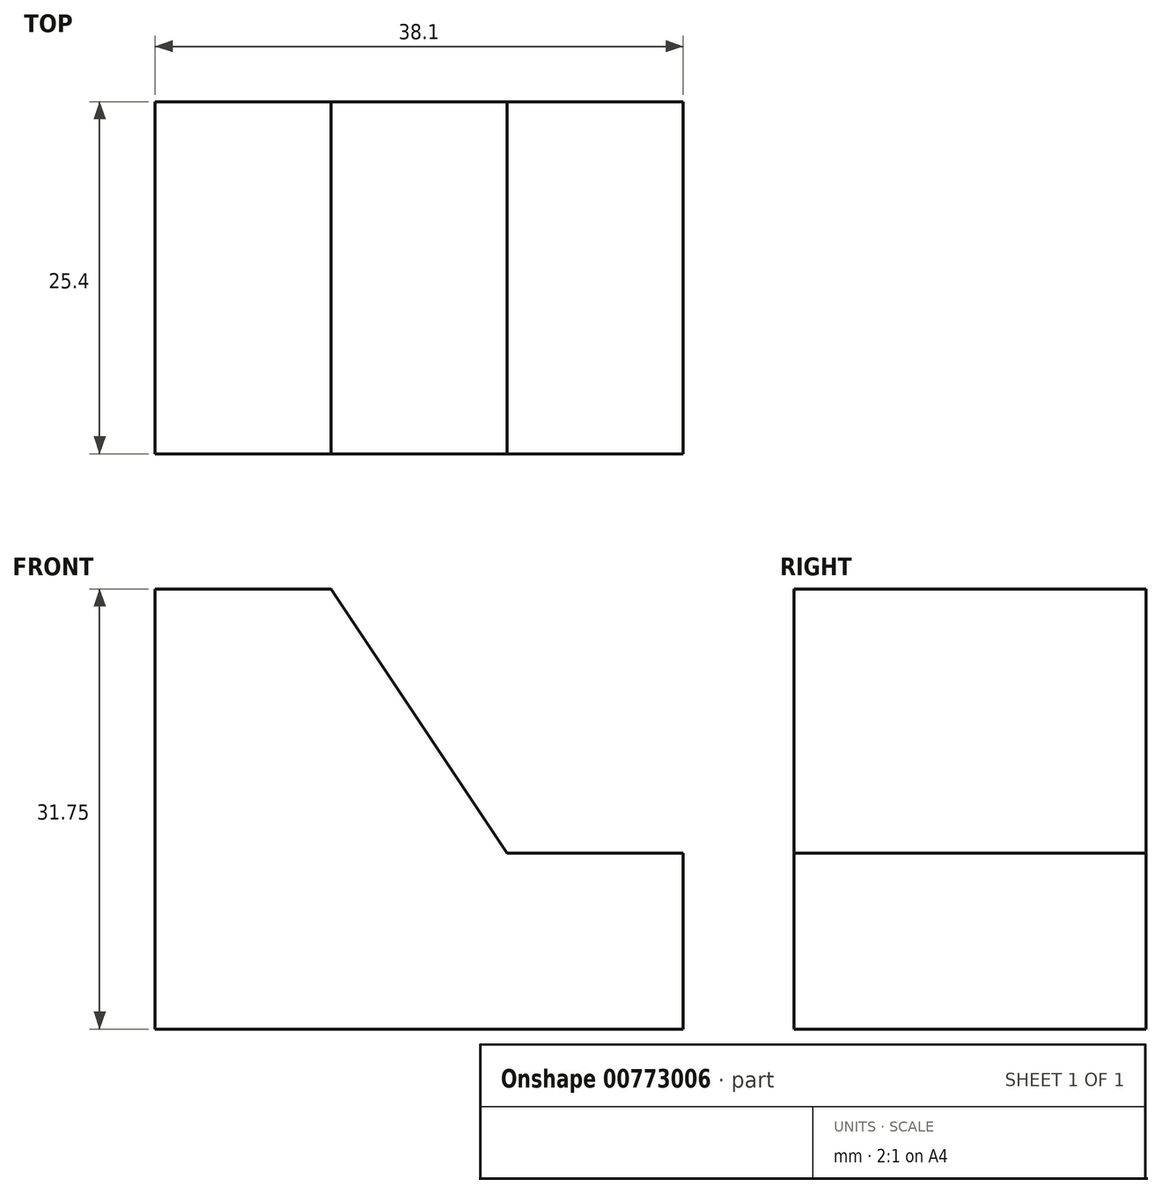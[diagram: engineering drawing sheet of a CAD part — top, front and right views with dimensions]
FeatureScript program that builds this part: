
annotation { "Feature Type Name" : "Feature", "Feature Type Description" : "" }
export const myFeature = defineFeature(function(context is Context, id is Id, definition is map)
    precondition{}
    {
        {
            var Q0;
            Q0=qCreatedBy(makeId("Front.planeOp"),FACE);
            var sketch = newSketch(context, id + "F0", { "sketchPlane" : qUnion([Q0])});
            skLineSegment(sketch, "E0", {"start": v(0, 0) * mm, "end": v(38.1, 0) * mm});
            skLineSegment(sketch, "E1", {"start": v(38.1, 0) * mm, "end": v(38.1, 31.75) * mm});
            skLineSegment(sketch, "E2", {"start": v(38.1, 31.75) * mm, "end": v(0, 31.75) * mm});
            skLineSegment(sketch, "E3", {"start": v(0, 31.75) * mm, "end": v(0, 0) * mm});
            skSolve(sketch);
        }
        {
            var Q0;
            Q0=makeQuery(id+"F0.imprint","IMPRINT",FACE,{"disambiguationData":[TD([[makeQuery(id+"F0.imprint","IMPRINT",EDGE,{"derivedFrom":sQuery(id+"F0.wireOp",EDGE,"E0")}),1.0]])]});
            extrude(context, id + "F1", {"entities" : qUnion([Q0]), "depth" : 25.4 * mm, "offsetDistance" : 25.4 * mm});
        }
        {
            var Q0;
            Q0=makeQuery(id+"F1.opExtrude","CAP_FACE",FACE,{"disambiguationData":[OSD([sQuery(id+"F0.wireOp",EDGE,"E0"),sQuery(id+"F0.wireOp",EDGE,"E1"),sQuery(id+"F0.wireOp",EDGE,"E2"),sQuery(id+"F0.wireOp",EDGE,"E3")])],"isStart":false});
            var sketch = newSketch(context, id + "F2", { "sketchPlane" : qUnion([Q0])});
            skLineSegment(sketch, "E4", {"start": v(0, 31.75) * mm, "end": v(12.7, 31.75) * mm});
            skLineSegment(sketch, "E5", {"start": v(38.1, 0) * mm, "end": v(38.1, 12.7) * mm});
            skLineSegment(sketch, "E6", {"start": v(38.1, 12.7) * mm, "end": v(25.4, 12.7) * mm});
            skLineSegment(sketch, "E7", {"start": v(25.4, 12.7) * mm, "end": v(12.7, 31.75) * mm});
            skSolve(sketch);
        }
        {
            var Q0;
            {var subQ0=sQuery(id+"F2.wireOp",EDGE,"E6");Q0=makeQuery(id+"F2.imprint","IMPRINT",FACE,{"disambiguationData":[TD([[makeQuery(id+"F2.imprint","IMPRINT",EDGE,{"derivedFrom":subQ0}),-1.0]])]});}
            extrude(context, id + "F3", {"entities" : qUnion([Q0]), "operationType" : NewBodyOperationType.REMOVE, "oppositeDirection" : true, "depth" : 25.4 * mm, "offsetDistance" : 25.4 * mm});
        }
    });
